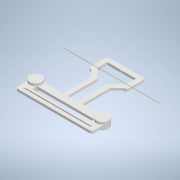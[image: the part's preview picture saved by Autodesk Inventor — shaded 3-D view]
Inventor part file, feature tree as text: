
AUTODESK INVENTOR PART (.ipt)
format: ipt  version: 2021.2 (Build 252289000, 289)  size: 296,960 bytes
history: native  units: in
note: dims shown in document units (in); Inventor stores cm internally (conversion verified against a paired STEP export)
features: sketch x10, hole x6, extrude x4, fillet x1, other x1
ambient origin geometry x8: Origin, YZ Plane, XZ Plane, XY Plane, X Axis, Y Axis, Z Axis, Center Point
bodies: Solid1 (feature_tree)
feature tree (22):
  extrude  "Extrusion1"  Depth=1.25in
  extrude  "Extrusion4"  Depth=0.25in
  extrude  "Extrusion5"  TaperAngle=45.0deg  [1 undecoded]
  fillet  "Fillet1"  Radius=0.1in
  hole  "Hole10"  [1 undecoded]
  hole  "Hole12"  [1 undecoded]
  hole  "Hole15"  [1 undecoded]
  hole  "Hole16"  [1 undecoded]
  hole  "Hole17"  [1 undecoded]
  hole  "Hole18"  [1 undecoded]
  extrude  "Extrusion7"  Depth=0.375in
  other  "Work Axis5"
  sketch  "Sketch1"  dims[d2=1.25in d3=1.25in]
  sketch  "Sketch6"  dims[d26=0.25in d27=0.0in d46=0.25in]
  sketch  "Sketch13"  dims[d55=0.1in d56=45.0deg d57=0.1in]
  sketch  "Sketch15"  dims[d58=45.0deg d59=0.1in]
  sketch  "Sketch17"  dims[d60=45.0deg d61=0.1in]
  sketch  "Sketch20"  dims[d62=45.0deg d63=0.25in d64=0.0in]
  sketch  "Sketch21"  dims[d119=1.0in d120=1.0in]
  sketch  "Sketch22"  dims[d121=2.0in d122=2.0in]
  sketch  "Sketch23"  dims[d123=135.0deg d124=45.0deg]
  sketch  "Sketch25"  dims[d130=1.25in d131=1.25in d132=0.25in d133=0.5in d134=0.0in d135=0.0in d143=1.0313in d144=0.2726in d145=0.375in d146=0.25in d147=0.5635in d148=0.5in d149=0.0in d157=0.9063in d158=0.2726in d159=0.375in d160=0.25in d161=0.5635in d162=0.125in d163=0.0in d182=3.874in d183=0.0in d184=3.874in d185=0.0in d186=0.0312in d187=0.2726in d188=0.375in d189=0.25in d190=0.5635in d191=0.125in d192=0.0in d193=3.749in d194=0.0in d195=0.0312in d196=0.2726in d197=0.375in d198=0.25in d199=0.5635in d200=0.125in d201=0.0in d202=3.749in d203=0.0in d204=3.624in d205=0.0in d206=3.624in d207=0.0in d208=0.0312in d209=0.2726in d210=0.375in d211=0.25in d212=0.5635in d213=0.125in d214=0.0in d215=3.249in d216=0.0in d217=3.249in d218=0.0in d219=0.0312in d220=0.2726in d221=0.375in d222=0.25in d223=0.5635in d224=0.125in d225=0.0in d229=0.125in d230=0.0in d28=0.5in d29=0.0344in d30=0.5in d31=0.0344in d47=1.0in d48=1.0in d49=1.0in d50=0.15in d51=0.25in d52=0.375in d53=0.5635in d54=0.75in d74=1.0in d75=1.0in d76=1.0in d77=0.15in d78=0.25in d79=0.375in d80=0.5635in d81=0.75in d82=0.8108in d83=0.0625in d84=0.75in d85=0.375in]
note: 7 required parameter values undecoded (feature->parameter linkage not recoverable at this tier; creation-order binding heuristic only, values carry confidence <= 0.55)
